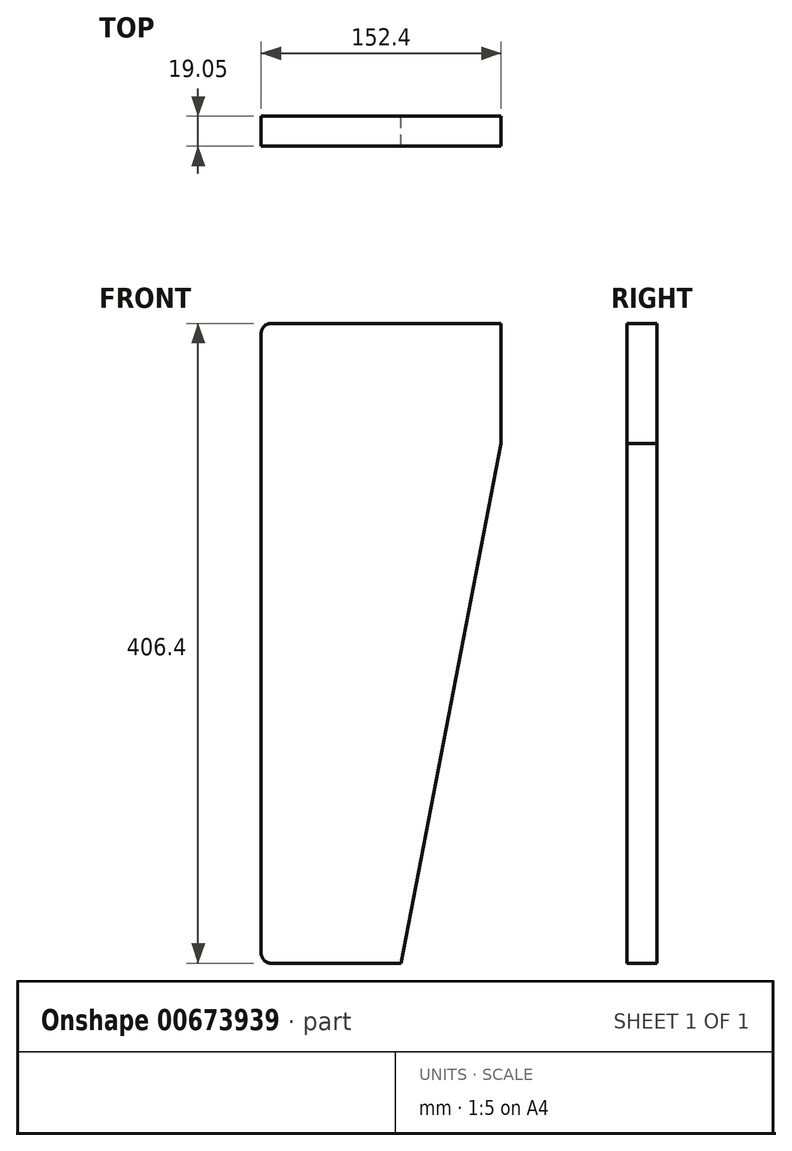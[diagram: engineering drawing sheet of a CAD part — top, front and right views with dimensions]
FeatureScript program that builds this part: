
annotation { "Feature Type Name" : "Feature", "Feature Type Description" : "" }
export const myFeature = defineFeature(function(context is Context, id is Id, definition is map)
    precondition{}
    {
        {
            var Q0;
            Q0=qCreatedBy(makeId("Front.planeOp"),FACE);
            var sketch = newSketch(context, id + "F0", { "sketchPlane" : qUnion([Q0])});
            skLineSegment(sketch, "E0.bottom", {"start": v(-379.5, 238) * mm, "end": v(-233.45, 238) * mm});
            skLineSegment(sketch, "E0.top", {"start": v(-379.5, -168.4) * mm, "end": v(-296.95, -168.4) * mm});
            skLineSegment(sketch, "E0.left", {"start": v(-385.85, 231.64) * mm, "end": v(-385.85, -162.06) * mm});
            skPoint(sketch, "E1.visualSharp", {"position": v(-385.85, 238) * mm});
            skArc(sketch, "E1.filletArc", {"start": v(-379.5, 238) * mm, "mid": v(-384, 236.14) * mm, "end": v(-385.85, 231.64) * mm});
            skPoint(sketch, "E2.visualSharp", {"position": v(-385.85, -168.4) * mm});
            skArc(sketch, "E2.filletArc", {"start": v(-385.85, -162.06) * mm, "mid": v(-384, -166.55) * mm, "end": v(-379.5, -168.4) * mm});
            skLineSegment(sketch, "E3", {"start": v(-296.95, -168.4) * mm, "end": v(-233.45, 161.8) * mm});
            skLineSegment(sketch, "E4", {"start": v(-233.45, 161.8) * mm, "end": v(-233.45, 238) * mm});
            skSolve(sketch);
        }
        {
            var Q0;
            Q0=makeQuery(id+"F0.imprint","IMPRINT",FACE,{"disambiguationData":[TD([[makeQuery(id+"F0.imprint","IMPRINT",EDGE,{"derivedFrom":sQuery(id+"F0.wireOp",EDGE,"E0.bottom")}),-1.0]])]});
            extrude(context, id + "F1", {"entities" : qUnion([Q0]), "depth" : 19.05 * mm, "offsetDistance" : 25.4 * mm});
        }
    });
